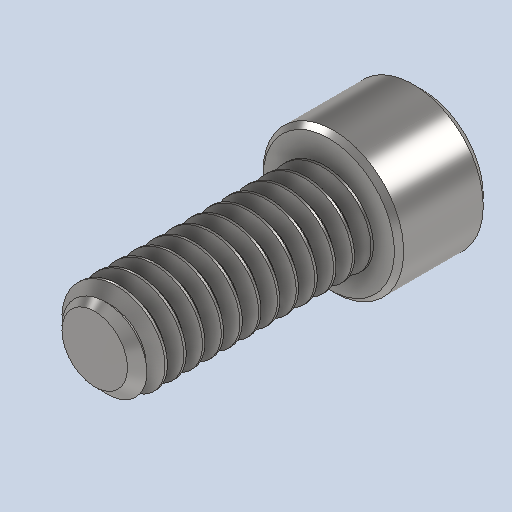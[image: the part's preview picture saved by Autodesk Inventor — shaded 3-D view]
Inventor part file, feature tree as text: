
AUTODESK INVENTOR PART (.ipt)
format: ipt  version: 2024 (Build 280153000, 153)  size: 590,336 bytes
history: native  units: in
note: dims shown in document units (in); Inventor stores cm internally (conversion verified against a paired STEP export)
features: chamfer x1
ambient origin geometry x8: Origin, YZ Plane, XZ Plane, XY Plane, X Axis, Y Axis, Z Axis, Center Point
bodies: Solid1 (feature_tree)
feature tree (1):
  chamfer  "Chamfer2"  [1 undecoded]
note: 1 required parameter value undecoded (feature->parameter linkage not recoverable at this tier; creation-order binding heuristic only, values carry confidence <= 0.55)
